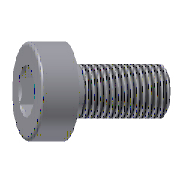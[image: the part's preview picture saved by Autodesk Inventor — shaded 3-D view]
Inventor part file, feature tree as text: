
AUTODESK INVENTOR PART (.ipt)
format: ipt  version: 2023.2 (Build 272271000, 271)  size: 172,544 bytes
history: native  units: mm
features: sketch x2
ambient origin geometry x8: Origin, YZ Plane, XZ Plane, XY Plane, X Axis, Y Axis, Z Axis, Center Point
bodies: Solid1 (feature_tree)
feature tree (2):
  sketch  "Sketch1"  dims[d0=13.0mm]
  sketch  "Sketch2"  dims[d1=8.0mm d2=8.0mm d3=35.0mm d4=10.297443mm d5=45.0deg d6=6.0mm d7=6.928203mm d8=4.0mm d44=90.0deg d45=10.0mm d9=0.0mm d10=22.0mm d11=0.0mm d12=0.625mm d50=2.0mm d51=45.0deg d13=0.625mm d14=0.0mm d15=0.0mm d55=0.0mm]
